annotation { "Feature Type Name" : "Feature", "Feature Type Description" : "" }
export const myFeature = defineFeature(function(context is Context, id is Id, definition is map)
    precondition{}
    {
        {
            var Q0;
            Q0=qCreatedBy(makeId("Front.planeOp"),FACE);
            var sketch = newSketch(context, id + "F0", { "sketchPlane" : qUnion([Q0])});
            skFitSpline(sketch, "E0", {"points": [v(-63.58, 40.22) * mm, v(-60.87, 41.68) * mm, v(-58.41, 41.89) * mm, v(-53.66, 40.06) * mm, v(-48.65, 38.97) * mm, v(-46.2, 37.77) * mm, v(-42.23, 33.49) * mm, v(-38.26, 31.34) * mm, v(-36.96, 31.14) * mm, v(-32.89, 29.83) * mm, v(-20.51, 22.73) * mm, v(-19.2, 21.37) * mm, v(-18.37, 20.38) * mm, v(-15.14, 19.29) * mm, v(-13.36, 17.63) * mm, v(-11.9, 15.45) * mm, v(-10.63, 14.47) * mm, v(-9.3, 14.41) * mm, v(-7.33, 15.4) * mm, v(-6.12, 15.86) * mm, v(-4.73, 15.63) * mm, v(-3.17, 15.05) * mm, v(-1.49, 14) * mm, v(0.48, 13.43) * mm, v(3.6, 13.37) * mm, v(6.5, 12.9) * mm, v(17.09, 6.14) * mm, v(19.73, 4.47) * mm, v(21.3, 3.04) * mm, v(24.78, -2.02) * mm, v(26.9, -2.77) * mm, v(28.4, -2.36) * mm, v(29.29, -1.2) * mm, v(30.72, 9.39) * mm, v(30.72, 16.5) * mm, v(31.4, 20.72) * mm, v(33.04, 23.8) * mm, v(35.16, 25.16) * mm, v(36.6, 24.96) * mm, v(37.34, 24.14) * mm, v(39.12, 22.43) * mm, v(40.83, 21.54) * mm, v(45.6, 21.13) * mm, v(47.45, 20.66) * mm, v(48.68, 19.63) * mm, v(49.91, 17.72) * mm, v(54.35, 13.21) * mm, v(56.2, 10.62) * mm, v(60.4, 7.36) * mm, v(65.5, 1.35) * mm, v(66.97, 0) * mm, v(67.77, -4.31) * mm, v(67.2, -6.58) * mm, v(67.88, -10.1) * mm, v(68, -14.74) * mm, v(67.2, -18.48) * mm, v(67.72, -27.98) * mm, v(63.93, -38.11) * mm, v(52.41, -47.35) * mm, v(50.19, -49.64) * mm, v(46.46, -51.7) * mm, v(42.19, -51.43) * mm, v(39.08, -49.57) * mm, v(37.63, -46.19) * mm, v(36.25, -44.32) * mm, v(34.4, -40.4) * mm, v(31.42, -31.42) * mm, v(29.09, -27.7) * mm, v(28.13, -26.07) * mm, v(27.12, -25.32) * mm, v(25.9, -23.75) * mm, v(24.1, -21.53) * mm, v(19.95, -21.44) * mm, v(16.53, -18.14) * mm, v(13.87, -14.74) * mm, v(12.43, -14.28) * mm, v(8.65, -14.25) * mm, v(5.55, -12.15) * mm, v(-1.33, -11.75) * mm, v(-4, -10.18) * mm, v(-8.27, -9.43) * mm, v(-14.22, -6.57) * mm, v(-16.38, 3.64) * mm, v(-23.47, 7.04) * mm, v(-29.13, 8.82) * mm, v(-34.54, 15.57) * mm, v(-39.73, 16.63) * mm, v(-43.68, 17.85) * mm, v(-45.99, 18.24) * mm, v(-49.94, 20.2) * mm, v(-51.33, 21.02) * mm, v(-54.5, 21.46) * mm, v(-57.73, 23.67) * mm, v(-59.64, 25.5) * mm, v(-62.33, 29.85) * mm, v(-63.15, 30.53) * mm, v(-64.37, 33.33) * mm, v(-63.58, 40.22) * mm]});
            skSolve(sketch);
        }
        {
            var Q0;
            Q0=qCreatedBy(makeId("Front.planeOp"),FACE);
            var sketch = newSketch(context, id + "F1", { "sketchPlane" : qUnion([Q0])});
            skFitSpline(sketch, "E1", {"points": [v(-59, 37.11) * mm, v(-57.96, 37.39) * mm, v(-54.25, 37.36) * mm, v(-48.47, 35.66) * mm, v(-43.56, 33.17) * mm, v(-41.26, 31.75) * mm, v(-39.22, 30.4) * mm, v(-37.69, 29.55) * mm, v(-35.36, 28.74) * mm, v(-33.93, 28.5) * mm, v(-32.48, 27.8) * mm, v(-29.7, 25.9) * mm, v(-28.44, 25.23) * mm, v(-26.3, 24.63) * mm, v(-24.2, 23.15) * mm, v(-18.68, 19.16) * mm, v(-13.13, 14.59) * mm, v(-12.05, 13.85) * mm, v(-10.1, 13.63) * mm, v(-7, 13.66) * mm, v(4.6, 10.06) * mm, v(10.18, 7.23) * mm, v(13.26, 5.68) * mm, v(22.74, -0.96) * mm, v(24.6, -2.9) * mm, v(25.75, -3.55) * mm, v(27.09, -3.77) * mm, v(28.73, -3.4) * mm, v(30.44, -2.43) * mm, v(31.54, -0.81) * mm, v(32.09, 2.06) * mm, v(32.77, 14.62) * mm, v(33.81, 17.03) * mm, v(34.75, 17.86) * mm, v(36.22, 18.18) * mm, v(37.56, 18.18) * mm, v(41.37, 16.89) * mm, v(54.69, 5.88) * mm, v(60.17, -8.44) * mm, v(60.87, -12.77) * mm, v(62.1, -16.75) * mm, v(62.23, -18.2) * mm, v(61.42, -20.46) * mm, v(60.42, -21.32) * mm, v(58.93, -21.72) * mm, v(55.76, -21.81) * mm, v(52.28, -22.18) * mm, v(50.97, -22.22) * mm, v(45.63, -23.53) * mm, v(43.78, -23.85) * mm, v(41.6, -23.9) * mm, v(37.99, -24.84) * mm, v(34.96, -26.52) * mm, v(33.83, -26.7) * mm, v(32.6, -26.3) * mm, v(32.06, -25.43) * mm, v(30.53, -22.4) * mm, v(28.47, -20.03) * mm, v(26, -19.73) * mm, v(21.73, -17.67) * mm, v(19.57, -17) * mm, v(11.4, -10.7) * mm, v(7.01, -9.62) * mm, v(0.77, -8.8) * mm, v(-9.25, -5.37) * mm, v(-10.77, -4.45) * mm, v(-12.88, -1.24) * mm, v(-15.4, 4.52) * mm, v(-17.04, 6.91) * mm, v(-18.72, 8.35) * mm, v(-25.32, 9.73) * mm, v(-29.56, 12.5) * mm, v(-35.04, 18.42) * mm, v(-40.05, 20.22) * mm, v(-42.44, 20.26) * mm, v(-46.82, 21.6) * mm, v(-47.63, 21.88) * mm, v(-48.43, 21.83) * mm, v(-51.76, 23.11) * mm, v(-55.4, 25.78) * mm, v(-58.63, 28.96) * mm, v(-60.2, 32.34) * mm, v(-60.4, 35.34) * mm, v(-59, 37.11) * mm]});
            skSolve(sketch);
        }
        {
            var Q0;
            Q0=qCreatedBy(makeId("Front.planeOp"),FACE);
            var sketch = newSketch(context, id + "F2", { "sketchPlane" : qUnion([Q0])});
            skFitSpline(sketch, "E2", {"points": [v(-55.95, 32.83) * mm, v(-55.02, 33.18) * mm, v(-53.66, 32.74) * mm, v(-53.04, 32.28) * mm, v(-52.2, 31.93) * mm, v(-51.44, 31.46) * mm, v(-50.7, 31.25) * mm, v(-47.98, 29.74) * mm, v(-46.23, 28.61) * mm, v(-45.34, 28.09) * mm, v(-44.86, 27.74) * mm, v(-43.5, 27) * mm, v(-41.37, 25.87) * mm, v(-36.62, 24.41) * mm, v(-33.04, 22.5) * mm, v(-31.41, 21.53) * mm, v(-29.23, 20.74) * mm, v(-25.63, 18.34) * mm, v(-24.4, 17.79) * mm, v(-19.76, 14.68) * mm, v(-18.56, 13.68) * mm, v(-17.27, 12.86) * mm, v(-13.33, 11.27) * mm, v(-10.67, 10.94) * mm, v(-9.02, 10.92) * mm, v(-4.4, 9.26) * mm, v(-3.04, 8.82) * mm, v(2.72, 7.49) * mm, v(18.03, 0.45) * mm, v(24.25, -3.86) * mm, v(26.84, -5) * mm, v(31.94, -5.03) * mm, v(35.4, -3.41) * mm, v(37.95, -0.84) * mm, v(39.5, 1.6) * mm, v(40.3, 3.98) * mm, v(40.22, 8.1) * mm, v(40.6, 9.28) * mm, v(41.1, 9.94) * mm, v(43.33, 9.54) * mm, v(49.38, 4.22) * mm, v(53.14, 1.1) * mm, v(55.63, -1.82) * mm, v(56.91, -5.2) * mm, v(56.79, -9.7) * mm, v(55.36, -13.51) * mm, v(51.94, -16.85) * mm, v(46.55, -18.82) * mm, v(34.8, -19.55) * mm, v(29.95, -18.23) * mm, v(25.98, -15.52) * mm, v(20.58, -12.4) * mm, v(12.95, -9.05) * mm, v(1.85, -3.54) * mm, v(-0.6, -2.56) * mm, v(-4.34, -1.08) * mm, v(-7.57, 1.81) * mm, v(-8.78, 4.2) * mm, v(-10.36, 6.29) * mm, v(-11.95, 7.48) * mm, v(-16.46, 9.27) * mm, v(-21.21, 12.27) * mm, v(-24.08, 13.74) * mm, v(-27.62, 15.94) * mm, v(-32.81, 20.46) * mm, v(-37.63, 23.3) * mm, v(-44.97, 26.23) * mm, v(-46.62, 27.08) * mm, v(-48.6, 28.52) * mm, v(-52.73, 30.28) * mm, v(-54.6, 30.64) * mm, v(-56.2, 31.97) * mm, v(-55.95, 32.83) * mm]});
            skSolve(sketch);
        }
        {
            var Q0;
            Q0=qCreatedBy(makeId("Front.planeOp"),FACE);
            var sketch = newSketch(context, id + "F3", { "sketchPlane" : qUnion([Q0])});
            skFitSpline(sketch, "E3", {"points": [v(3.91, 3.61) * mm, v(5.2, 3.61) * mm, v(11.6, 1.54) * mm, v(16.22, -0.83) * mm, v(20.49, -3.52) * mm, v(24.63, -5.59) * mm, v(28.53, -7) * mm, v(35.79, -7.54) * mm, v(39.93, -6.38) * mm, v(41.94, -4.68) * mm, v(43.77, -1.68) * mm, v(45.49, -0.35) * mm, v(49.09, -0.21) * mm, v(51.8, -2.15) * mm, v(53.3, -4.88) * mm, v(52.7, -8.24) * mm, v(50.7, -10.73) * mm, v(44.93, -13.69) * mm, v(39.3, -14.59) * mm, v(31.75, -13.04) * mm, v(8.15, -2.87) * mm, v(4.4, -1.58) * mm, v(1.8, 0.43) * mm, v(2.35, 2.9) * mm, v(3.91, 3.61) * mm]});
            skSolve(sketch);
        }
        {
            var Q0;
            Q0=qCreatedBy(makeId("Front.planeOp"),FACE);
            var sketch = newSketch(context, id + "F4", { "sketchPlane" : qUnion([Q0])});
            skFitSpline(sketch, "E4", {"points": [v(31.95, -9.96) * mm, v(32.15, -9.27) * mm, v(33.98, -8.49) * mm, v(35.98, -8.1) * mm, v(38.87, -8.11) * mm, v(42.6, -7.63) * mm, v(43.74, -7.45) * mm, v(45.42, -8.18) * mm, v(45.76, -9.74) * mm, v(45.3, -10.89) * mm, v(44.18, -11.89) * mm, v(39.46, -12.01) * mm, v(35.93, -11.92) * mm, v(33.35, -11.42) * mm, v(31.95, -9.96) * mm]});
            skSolve(sketch);
        }
        {
            var Q0;
            Q0=qCreatedBy(makeId("Front.planeOp"),FACE);
            var sketch = newSketch(context, id + "F5", { "sketchPlane" : qUnion([Q0])});
            skLineSegment(sketch, "E5.bottom", {"start": v(-68.5, 45.68) * mm, "end": v(71.01, 45.68) * mm});
            skLineSegment(sketch, "E5.top", {"start": v(-68.5, -55.85) * mm, "end": v(71.01, -55.85) * mm});
            skLineSegment(sketch, "E5.left", {"start": v(-68.5, 45.68) * mm, "end": v(-68.5, -55.85) * mm});
            skLineSegment(sketch, "E5.right", {"start": v(71.01, 45.68) * mm, "end": v(71.01, -55.85) * mm});
            skSolve(sketch);
        }
        {
            var Q0;
            Q0=makeQuery(id+"F5.imprint","IMPRINT",FACE,{"disambiguationData":[TD([[makeQuery(id+"F5.imprint","IMPRINT",EDGE,{"derivedFrom":sQuery(id+"F5.wireOp",EDGE,"E5.bottom")}),-1.0]])]});
            extrude(context, id + "F6", {"entities" : qUnion([Q0]), "depth" : -10 * mm});
        }
        {
            var Q0;
            Q0 = qSketchRegion(id + "F0", true);
            extrude(context, id + "F7", {"entities" : qUnion([Q0]), "operationType" : NewBodyOperationType.REMOVE, "oppositeDirection" : true, "depth" : 1 * mm});
        }
        {
            var Q0;
            Q0=makeQuery(id+"F1.imprint","IMPRINT",FACE,{"disambiguationData":[TD([[makeQuery(id+"F1.imprint","IMPRINT",EDGE,{"derivedFrom":sQuery(id+"F1.wireOp",EDGE,"E1")}),-1.0]])]});
            extrude(context, id + "F8", {"entities" : qUnion([Q0]), "operationType" : NewBodyOperationType.REMOVE, "oppositeDirection" : true, "depth" : 2 * mm});
        }
        {
            var Q0;
            Q0=makeQuery(id+"F2.imprint","IMPRINT",FACE,{"disambiguationData":[TD([[makeQuery(id+"F2.imprint","IMPRINT",EDGE,{"derivedFrom":sQuery(id+"F2.wireOp",EDGE,"E2")}),-1.0]])]});
            extrude(context, id + "F9", {"entities" : qUnion([Q0]), "operationType" : NewBodyOperationType.REMOVE, "oppositeDirection" : true, "depth" : 3 * mm});
        }
        {
            var Q0;
            Q0=makeQuery(id+"F3.imprint","IMPRINT",FACE,{"disambiguationData":[TD([[makeQuery(id+"F3.imprint","IMPRINT",EDGE,{"derivedFrom":sQuery(id+"F3.wireOp",EDGE,"E3")}),-1.0]])]});
            extrude(context, id + "F10", {"entities" : qUnion([Q0]), "operationType" : NewBodyOperationType.REMOVE, "oppositeDirection" : true, "depth" : 4 * mm});
        }
        {
            var Q0;
            Q0=makeQuery(id+"F4.imprint","IMPRINT",FACE,{"disambiguationData":[TD([[makeQuery(id+"F4.imprint","IMPRINT",EDGE,{"derivedFrom":sQuery(id+"F4.wireOp",EDGE,"E4")}),-1.0]])]});
            extrude(context, id + "F11", {"entities" : qUnion([Q0]), "operationType" : NewBodyOperationType.REMOVE, "oppositeDirection" : true, "depth" : 5 * mm});
        }
        {
            var Q0;
            Q0=qCreatedBy(makeId("Front.planeOp"),FACE);
            var sketch = newSketch(context, id + "F12", { "sketchPlane" : qUnion([Q0])});
            skText(sketch, "E6", { "text": "THUNDER LAKE", "fontName": "RobotoSlab-Bold.ttf"});
            skText(sketch, "E7", { "text": "Area: 63 Acres", "fontName": "OpenSans-Regular.ttf"});
            skText(sketch, "E8", { "text": "Shore: 1.9 Miles", "fontName": "OpenSans-Regular.ttf"});
            const initialGuessF12  = {"E6": [-0.06273, -0.03322, 1, 0, 0.007], "E7": [-0.04317, -0.04569, 1, 0, 0.003], "E8": [-0.04483, -0.04986, 1, 0, 0.003]};
            skSetInitialGuess(sketch, initialGuessF12);
            skSolve(sketch);
        }
        {
            var Q0;
            Q0 = qSketchRegion(id + "F12", true);
            extrude(context, id + "F13", {"entities" : qUnion([Q0]), "operationType" : NewBodyOperationType.REMOVE, "oppositeDirection" : true, "depth" : 5 * mm});
        }
        {
            var Q0;
            Q0=makeQuery(id+"F6.opExtrude","CAP_FACE",FACE,{"disambiguationData":[OSD([sQuery(id+"F5.wireOp",EDGE,"E5.bottom"),sQuery(id+"F5.wireOp",EDGE,"E5.top"),sQuery(id+"F5.wireOp",EDGE,"E5.left"),sQuery(id+"F5.wireOp",EDGE,"E5.right")])],"isStart":false});
            cPlane(context, id + "F14", {"entities" : qUnion([Q0]), "cplaneType" : CPlaneType.OFFSET, "offset" : 1.6 * mm, "oppositeDirection" : true, "width" : 150 * mm, "height" : 150 * mm});
        }
        {
            var Q0;
            Q0=qCreatedBy(id+"F14.planeOp",FACE);
            var sketch = newSketch(context, id + "F15", { "sketchPlane" : qUnion([Q0])});
            skLineSegment(sketch, "E9", {"start": v(-2.6, 23.43) * mm, "end": v(-2.6, 28.16) * mm});
            skArc(sketch, "E10", {"start": v(2.74, 28.13) * mm, "mid": v(0.08, 29.83) * mm, "end": v(-2.6, 28.16) * mm});
            skLineSegment(sketch, "E11", {"start": v(2.74, 28.13) * mm, "end": v(2.74, 23.3) * mm});
            skArc(sketch, "E12", {"start": v(-2.6, 23.43) * mm, "mid": v(0, 20.77) * mm, "end": v(2.74, 23.3) * mm});
            skSolve(sketch);
        }
        {
            var Q0;
            Q0=makeQuery(id+"F6.opExtrude","CAP_FACE",FACE,{"disambiguationData":[OSD([sQuery(id+"F5.wireOp",EDGE,"E5.bottom"),sQuery(id+"F5.wireOp",EDGE,"E5.top"),sQuery(id+"F5.wireOp",EDGE,"E5.left"),sQuery(id+"F5.wireOp",EDGE,"E5.right")])],"isStart":false});
            var sketch = newSketch(context, id + "F16", { "sketchPlane" : qUnion([Q0])});
            skArc(sketch, "E13", {"start": v(-1.27, 25.8) * mm, "mid": v(0, 21.4) * mm, "end": v(1.27, 25.8) * mm});
            skLineSegment(sketch, "E14", {"start": v(1.27, 25.8) * mm, "end": v(1.27, 27.71) * mm});
            skLineSegment(sketch, "E15", {"start": v(-1.27, 27.71) * mm, "end": v(-1.27, 25.8) * mm});
            skArc(sketch, "E16", {"start": v(1.27, 27.71) * mm, "mid": v(0, 28.99) * mm, "end": v(-1.27, 27.71) * mm});
            skLineSegment(sketch, "E17", {"start": v(-1.27, 25.8) * mm, "end": v(-0.56, 25.8) * mm});
            skLineSegment(sketch, "E18", {"start": v(1.27, 25.8) * mm, "end": v(0.56, 25.8) * mm});
            skArc(sketch, "E19", {"start": v(0.56, 27.71) * mm, "mid": v(0, 28.27) * mm, "end": v(-0.56, 27.71) * mm});
            skLineSegment(sketch, "E20", {"start": v(-0.56, 25.8) * mm, "end": v(-0.56, 27.71) * mm});
            skLineSegment(sketch, "E21", {"start": v(0.56, 25.8) * mm, "end": v(0.56, 27.71) * mm});
            skSolve(sketch);
        }
        {
            var Q0;
            Q0=makeQuery(id+"F16.imprint","IMPRINT",FACE,{"disambiguationData":[TD([[makeQuery(id+"F16.imprint","IMPRINT",EDGE,{"derivedFrom":sQuery(id+"F16.wireOp",EDGE,"E13")}),1.0]])]});
            extrude(context, id + "F17", {"entities" : qUnion([Q0]), "operationType" : NewBodyOperationType.REMOVE, "oppositeDirection" : true, "depth" : 5 * mm});
        }
        {
            var Q0;
            Q0=makeQuery(id+"F15.imprint","IMPRINT",FACE,{"disambiguationData":[TD([[makeQuery(id+"F15.imprint","IMPRINT",EDGE,{"derivedFrom":sQuery(id+"F15.wireOp",EDGE,"E9")}),-1.0]])]});
            var Q1;
            Q1=makeQuery(id+"F17.boolean.opBoolean","COPY",FACE,{"derivedFrom":makeQuery(id+"F17.opExtrude","CAP_FACE",FACE,{"disambiguationData":[OSD([sQuery(id+"F16.wireOp",EDGE,"E13"),sQuery(id+"F16.wireOp",EDGE,"E17"),sQuery(id+"F16.wireOp",EDGE,"E18"),sQuery(id+"F16.wireOp",EDGE,"E19"),sQuery(id+"F16.wireOp",EDGE,"E20"),sQuery(id+"F16.wireOp",EDGE,"E21")])],"isStart":false})});
            extrude(context, id + "F18", {"entities" : qUnion([Q0]), "operationType" : NewBodyOperationType.REMOVE, "endBound" : BoundingType.UP_TO_SURFACE, "oppositeDirection" : true, "endBoundEntityFace" : qUnion([Q1]), "depth" : 25 * mm});
        }
    });